# Revit family: Betonsteinplatte
name_source: partatom
category: Allgemeines Modell
revit_build: Autodesk Revit 2016 (Build: 20161004_0715(x64)
units: mm (PartAtom-declared; Revit-internal decimal feet)

## family parameters
Arbeitsebenenbasiert = Nein
Beim Laden mit Abzugskörper schneiden = Nein
Bemaßung runder Anschluss = Durchmesser verwenden
Gemeinsam genutzt = Nein
Immer vertikal = Ja
Kann Basisbauteil für Bewehrung sein = Nein
Raumberechnungspunkt = Nein
Teiletyp = Normal

## types (6) — shared parameters
Fasenausbildung = Minifase
Material = Natursteinvorsatz + Hinterbeton (zweischichtig)
Norm = DIN EN 12878
Oberflächenbearbeitung = geschliffen
Produktfamilie = Betonsteinplatte
Produktionsnorm = DIN EN 1339
Produktname = City-Schraffur
Produzent = Kronimus AG, Iffezheim
R-Wert  nach DIN 51130 = R11
Stations-Kategorie = 3-7
verfügbare Steindicke in mm = 80
www = www.kronimus.de

## per-type parameters (varying)
| type | Artikelnummer | Farbausführung | GTIN - Nummer | Hersteller | LRV-Wert | Materialität | Rastermaß L/ B in mm | Stein 1 | Stein 2 | Stein 2.1 | Systemstein |
| City-Schraffur 318/212  Stein 2.1 Anthrazit gesprenkelt | 2-426408-275-07 | Nr. 275 DB Anthrazit gesprenkelt | 4060851016946 | Kronimus AG, Iffezheim | 10,63 | Nr. 275 DB Anthrazit gesprenkelt | 318/212 | Nein | Nein | Ja | Stein 2.1 |
| City-Schraffur 318/212 Stein 2.1 Weiß gesprenkelt | 2-426408-276-07 | Nr. 276 DB Weiß gesprenkelt | 4060851016953 | Kronimus AG, Iffezheim | 62,7 | Nr. 276 DB Weiß gesprenkelt | 318/212 | Nein | Nein | Ja | Stein 2.1 |
| City-Schraffur 424/212 Stein 2 Weiß gesprenkelt | 2-426308-276-07 | Nr. 276 DB Weiß gesprenkelt | 4060851016939 | Kronimus AG, Iffezheim | 62,7 | Nr. 276 DB Weiß gesprenkelt | 424/212 | Nein | Ja | Nein | Stein 2 |
| City-Schraffur 424/212  Stein 1 Weiß gesprenkelt | 2-422108-276-07 | Nr. 276 DB Weiß gesprenkelt | 4060851016915 | Kronimus AG, Iffezheim | 62,7 | Nr. 276 DB Weiß gesprenkelt | 424/212 | Ja | Nein | Nein | Stein 1 |
| City-Schraffur 424/212  Stein 1 Anthrazit gesprenkelt | 2-422108-275-07 | Nr. 275 DB Anthrazit gesprenkelt | 4060851016908 | Kronimus AG, Iffezheim | 10,63 | Nr. 275 DB Anthrazit gesprenkelt | 424/212 | Ja | Nein | Nein | Stein 1 |
| City-Schraffur 424/212 Stein 2 Anthrazit gesprenkelt | 2-426308-275-07 | Nr. 275 DB Anthrazit gesprenkelt | 4060851016922 |  | 10,63 | Nr. 275 DB Anthrazit gesprenkelt | 424/212 | Nein | Ja | Nein | Stein2 |
